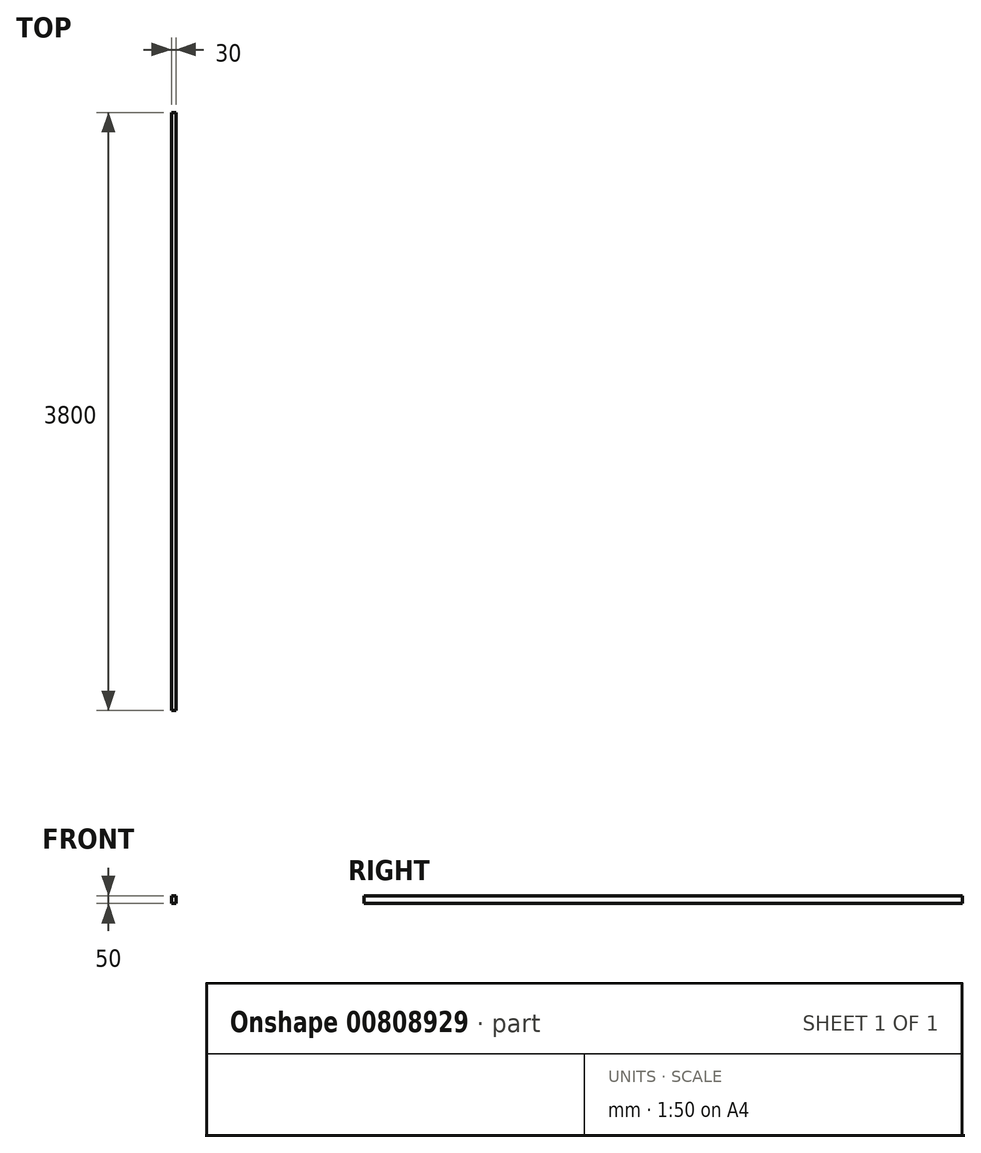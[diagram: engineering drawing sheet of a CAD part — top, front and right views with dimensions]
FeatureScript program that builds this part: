
annotation { "Feature Type Name" : "Feature", "Feature Type Description" : "" }
export const myFeature = defineFeature(function(context is Context, id is Id, definition is map)
    precondition{}
    {
        {
            var Q0;
            Q0=qCreatedBy(makeId("Front.planeOp"),FACE);
            var sketch = newSketch(context, id + "F0", { "sketchPlane" : qUnion([Q0])});
            skLineSegment(sketch, "E0.bottom", {"start": v(0, 0) * mm, "end": v(30, 0) * mm});
            skLineSegment(sketch, "E0.top", {"start": v(0, 50) * mm, "end": v(30, 50) * mm});
            skLineSegment(sketch, "E0.left", {"start": v(0, 0) * mm, "end": v(0, 50) * mm});
            skLineSegment(sketch, "E0.right", {"start": v(30, 0) * mm, "end": v(30, 50) * mm});
            skSolve(sketch);
        }
        {
            var Q0;
            Q0=qSketchRegion(id+"F0",true);
            extrude(context, id + "F1", {"entities" : qUnion([Q0]), "oppositeDirection" : true, "depth" : 3800 * mm, "offsetDistance" : 25 * mm});
        }
    });
